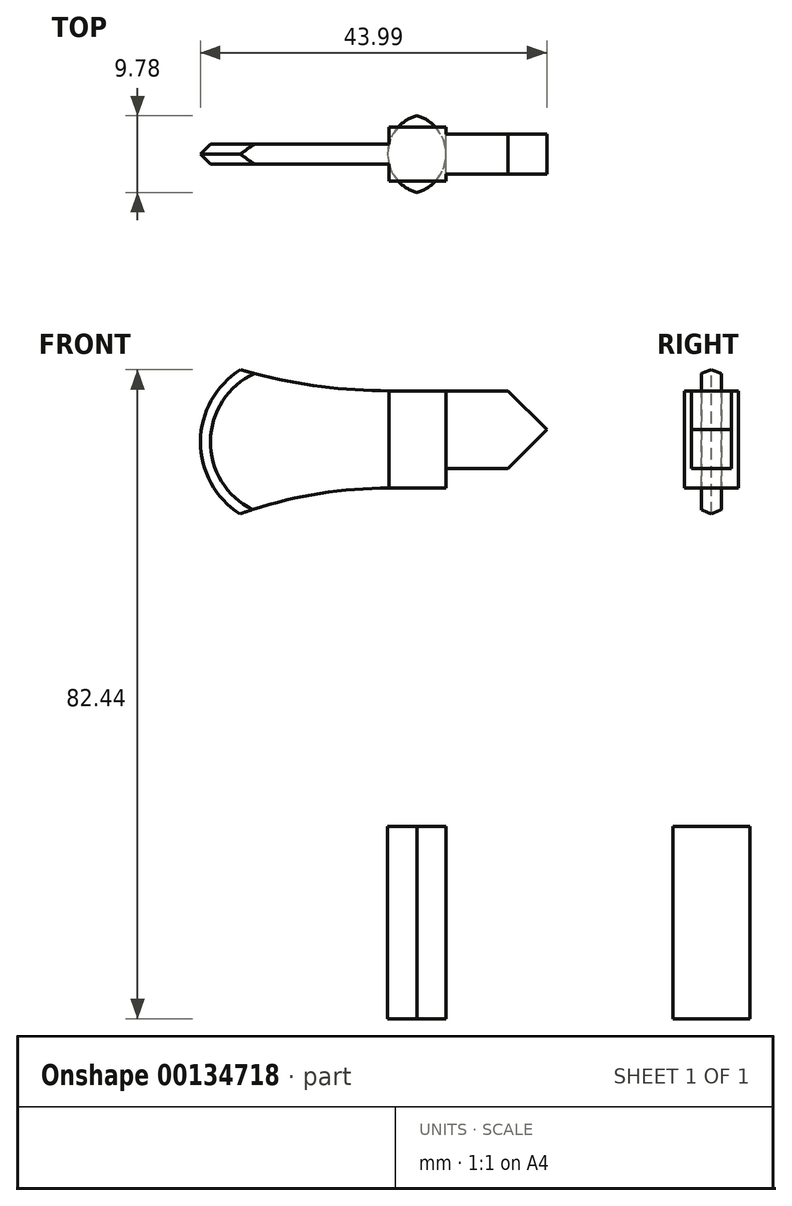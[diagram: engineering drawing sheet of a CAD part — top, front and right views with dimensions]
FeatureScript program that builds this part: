
annotation { "Feature Type Name" : "Feature", "Feature Type Description" : "" }
export const myFeature = defineFeature(function(context is Context, id is Id, definition is map)
    precondition{}
    {
        {
            var Q0;
            Q0=qCreatedBy(makeId("Front.planeOp"),FACE);
            var sketch = newSketch(context, id + "F0", { "sketchPlane" : qUnion([Q0])});
            skLineSegment(sketch, "E0.bottom", {"start": v(-7.4, 10.85) * mm, "end": v(0, 10.85) * mm});
            skLineSegment(sketch, "E0.top", {"start": v(-7.4, -63.69) * mm, "end": v(0, -63.69) * mm});
            skLineSegment(sketch, "E0.left", {"start": v(-7.4, 10.85) * mm, "end": v(-7.4, -63.69) * mm});
            skLineSegment(sketch, "E0.right", {"start": v(0, 10.85) * mm, "end": v(0, -63.69) * mm});
            skLineSegment(sketch, "E1", {"start": v(-7.4, -39.27) * mm, "end": v(0, -39.27) * mm});
            skLineSegment(sketch, "E2", {"start": v(-3.92, 0) * mm, "end": v(-3.92, -39.27) * mm});
            skSolve(sketch);
        }
        {
            var Q0;
            Q0=qCreatedBy(makeId("Front.planeOp"),FACE);
            var sketch = newSketch(context, id + "F1", { "sketchPlane" : qUnion([Q0])});
            skLineSegment(sketch, "E3.bottom", {"start": v(-7.21, 3.72) * mm, "end": v(0, 3.72) * mm});
            skLineSegment(sketch, "E3.top", {"start": v(-7.21, 16.07) * mm, "end": v(0, 16.07) * mm});
            skLineSegment(sketch, "E3.left", {"start": v(-7.21, 3.72) * mm, "end": v(-7.21, 16.07) * mm});
            skLineSegment(sketch, "E3.right", {"start": v(0, 3.72) * mm, "end": v(0, 16.07) * mm});
            skArc(sketch, "E4", {"start": v(-27.34, 19.13) * mm, "mid": v(-17.4, 16.84) * mm, "end": v(-7.21, 16.07) * mm});
            skArc(sketch, "E5", {"start": v(-27.34, 19.13) * mm, "mid": v(-32.2, 9.57) * mm, "end": v(-27.34, 0) * mm});
            skArc(sketch, "E6", {"start": v(-7.21, 3.72) * mm, "mid": v(-17.45, 2.78) * mm, "end": v(-27.34, 0) * mm});
            skLineSegment(sketch, "E7.bottom", {"start": v(0, 16.07) * mm, "end": v(0, 16.07) * mm});
            skLineSegment(sketch, "E7.top", {"start": v(0, 3.72) * mm, "end": v(0, 3.72) * mm});
            skLineSegment(sketch, "E7.left", {"start": v(0, 16.07) * mm, "end": v(0, 3.72) * mm});
            skLineSegment(sketch, "E8.bottom", {"start": v(0, 16.07) * mm, "end": v(12.96, 16.07) * mm});
            skLineSegment(sketch, "E8.top", {"start": v(0, 6.2) * mm, "end": v(12.96, 6.2) * mm});
            skLineSegment(sketch, "E8.left", {"start": v(0, 16.07) * mm, "end": v(0, 6.2) * mm});
            skLineSegment(sketch, "E8.right", {"start": v(12.96, 16.07) * mm, "end": v(12.96, 6.2) * mm});
            skSolve(sketch);
        }
        {
            var Q0;
            {var subQ0=sQuery(id+"F0.wireOp",EDGE,"E0.top");Q0=makeQuery(id+"F0.imprint","IMPRINT",FACE,{"disambiguationData":[TD([[makeQuery(id+"F0.imprint","IMPRINT",EDGE,{"derivedFrom":subQ0}),1.0]])]});}
            extrude(context, id + "F2", {"entities" : qUnion([Q0]), "endBound" : BoundingType.SYMMETRIC, "depth" : 10.16 * mm});
        }
        {
            var Q0;
            Q0=makeQuery(id+"F2.opExtrude","CAP_EDGE",EDGE,{"disambiguationData":[OSD([sQuery(id+"F0.wireOp",EDGE,"E0.left")])],"isStart":false});
            var Q1;
            Q1=makeQuery(id+"F2.opExtrude","CAP_EDGE",EDGE,{"disambiguationData":[OSD([sQuery(id+"F0.wireOp",EDGE,"E0.right")])],"isStart":false});
            var Q2;
            Q2=makeQuery(id+"F2.opExtrude","CAP_EDGE",EDGE,{"disambiguationData":[OSD([sQuery(id+"F0.wireOp",EDGE,"E0.right")])],"isStart":true});
            var Q3;
            Q3=makeQuery(id+"F2.opExtrude","CAP_EDGE",EDGE,{"disambiguationData":[OSD([sQuery(id+"F0.wireOp",EDGE,"E0.left")])],"isStart":true});
            fillet(context, id + "F3", {"entities" : qUnion([Q0, Q1, Q2, Q3]), "radius" : 5.08 * mm, "tangentPropagation" : true, "allowEdgeOverflow" : false});
        }
        {
            var Q0;
            Q0=sQuery(id+"F0.wireOp",EDGE,"E0.left");
            var Q1;
            Q1=sQuery(id+"F0.wireOp",EDGE,"E2");
            revolve(context, id + "F4", {"bodyType" : ToolBodyType.SURFACE, "surfaceEntities" : qUnion([Q0]), "axis" : qUnion([Q1]), "revolveType" : RevolveType.FULL});
        }
        {
            var Q0;
            Q0=makeQuery(id+"F1.imprint","IMPRINT",FACE,{"disambiguationData":[TD([[makeQuery(id+"F1.imprint","IMPRINT",EDGE,{"derivedFrom":sQuery(id+"F1.wireOp",EDGE,"E3.bottom")}),1.0]])]});
            extrude(context, id + "F5", {"entities" : qUnion([Q0]), "endBound" : BoundingType.SYMMETRIC, "depth" : 6.86 * mm});
        }
        {
            var Q0;
            Q0=makeQuery(id+"F1.imprint","IMPRINT",FACE,{"disambiguationData":[TD([[makeQuery(id+"F1.imprint","IMPRINT",EDGE,{"derivedFrom":sQuery(id+"F1.wireOp",EDGE,"E3.left")}),1.0]])]});
            extrude(context, id + "F6", {"entities" : qUnion([Q0]), "operationType" : NewBodyOperationType.ADD, "endBound" : BoundingType.SYMMETRIC, "depth" : 2.54 * mm});
        }
        {
            var Q0;
            Q0=makeQuery(id+"F6.opExtrude","CAP_EDGE",EDGE,{"disambiguationData":[OSD([sQuery(id+"F1.wireOp",EDGE,"E5")])],"isStart":false});
            var Q1;
            Q1=makeQuery(id+"F6.opExtrude","CAP_EDGE",EDGE,{"disambiguationData":[OSD([sQuery(id+"F1.wireOp",EDGE,"E5")])],"isStart":true});
            chamfer(context, id + "F7", {"entities" : qUnion([Q0, Q1]), "width" : 2.3 * mm, "tangentPropagation" : true});
        }
        {
            var Q0;
            Q0=makeQuery(id+"F1.imprint","IMPRINT",FACE,{"disambiguationData":[TD([[makeQuery(id+"F1.imprint","IMPRINT",EDGE,{"derivedFrom":sQuery(id+"F1.wireOp",EDGE,"E8.bottom")}),-1.0]])]});
            extrude(context, id + "F8", {"entities" : qUnion([Q0]), "operationType" : NewBodyOperationType.ADD, "endBound" : BoundingType.SYMMETRIC, "depth" : 5.08 * mm});
        }
        {
            var Q0;
            Q0=makeQuery(id+"F8.opExtrude","SWEPT_EDGE",EDGE,{"disambiguationData":[OSD([sQuery(id+"F1.wireOp",EDGE,"E8.bottom"),sQuery(id+"F1.wireOp",EDGE,"E8.right")])]});
            var Q1;
            Q1=makeQuery(id+"F8.opExtrude","SWEPT_EDGE",EDGE,{"disambiguationData":[OSD([sQuery(id+"F1.wireOp",EDGE,"E8.top"),sQuery(id+"F1.wireOp",EDGE,"E8.right")])]});
            chamfer(context, id + "F9", {"entities" : qUnion([Q0, Q1]), "width" : 5.08 * mm, "tangentPropagation" : true});
        }
    });
